# Revit family: Sigma_Compact_DN200-LF_PN16_RFA_2018
name_source: partatom
category: Pipe Accessories
revit_build: Autodesk Revit LT 2018 (Build: 20180329_1100(x64)
units: mm (PartAtom-declared; Revit-internal decimal feet)

## family parameters
Always vertical = Yes
Cut with Voids When Loaded = No
Part Type = Valve - Breaks Into
Round Connector Dimension = Use Diameter
Shared = No
Work Plane-Based = No

## types (9) — shared parameters
CAT0 = Yes
Description = Automatický vyvažovací ventil
H6 = 85 mm
L2D = 230 mm
L2D_Min = 30 mm  [stored 0.0984252 ft]
MC Pressure Drop Maximum Value = 0.0 Pa
MC Pressure Drop Minimum Value = 0.0 Pa
MC Use Limits From Balancing Method = No
Manufacturer = Hydronix
QmdConnectorList = 301;D;302;D
URL = www.hydronix.cz
W2D = 50 mm
magiPartTypeId = 304
magiProductFamilyId = 111bdfd32e424cd9a1e5f1ca7ea2b6
zero-valued in all types: MC Throttling Maximum Value, MC Throttling Minimum Value

## per-type parameters (varying)
- Sigma Compact DN 050 LF PN16: D=50 mm; DF2=83 mm; H=367 mm; H1=480 mm; H11=124 mm; H2=62 mm; H3=21 mm; H4=25 mm  [stored 0.082021 ft]; HDF=202 mm; HDF__ve=-202 mm  [stored -0.66273 ft]; HH1=33 mm  [stored 0.108268 ft]; HH12=17 mm; L2=115 mm; L3=193 mm; L4=108 mm; L42=54 mm; L43=38 mm; L432=19 mm; LF=18 mm; LF2=9 mm; LF__ve=-18 mm; MC Product Code=53-2400 DN50; PN16; (2480-15000 l/h); kvs=34; R1=58 mm; R3=43 mm; R4=40 mm; Type Comments=přírubový; PN16; max dp=800kPa; 0~+120°C; max uzavírací tlak 1MPa; magiProductId=7ce002c265594233b83d195dc264f1
- Sigma Compact DN 065 LF PN16: D=65 mm; DF2=93 mm; H=384 mm; H1=497 mm; H11=139 mm; H2=69 mm; H3=23 mm; H4=28 mm  [stored 0.0918635 ft]; HDF=199 mm; HDF__ve=-199 mm  [stored -0.652887 ft]; HH1=33 mm  [stored 0.108268 ft]; HH12=17 mm; L2=145 mm; L3=244 mm; L4=136 mm; L42=68 mm; L43=48 mm; L432=24 mm  [stored 0.0787402 ft]; LF=23 mm; LF2=12 mm  [stored 0.0393701 ft]; LF__ve=-23 mm; MC Product Code=53-2401 DN65; PN16; (4380-25000 l/h); kvs=50; R1=73 mm; R3=48 mm; R4=51 mm; Type Comments=přírubový; PN16; max dp=800kPa; 0~+120°C; max uzavírací tlak 1MPa; magiProductId=7b440009bc83499eb1c9a6fd3b4fee
- Sigma Compact DN 080 LF PN16: D=80 mm; DF2=100 mm; H=413 mm; H1=526 mm; H11=150 mm; H2=75 mm; H3=25 mm  [stored 0.082021 ft]; H4=30 mm  [stored 0.0984252 ft]; HDF=213 mm; HDF__ve=-213 mm  [stored -0.698819 ft]; HH1=33 mm  [stored 0.108268 ft]; HH12=17 mm; L2=155 mm; L3=260 mm; L4=146 mm; L42=73 mm; L43=51 mm; L432=25 mm  [stored 0.082021 ft]; LF=25 mm  [stored 0.082021 ft]; LF2=12 mm  [stored 0.0393701 ft]; LF__ve=-25 mm  [stored -0.082021 ft]; MC Product Code=53-2402 DN80; PN16; (5340-34000 l/h); kvs=68; R1=78 mm; R3=52 mm; R4=54 mm; Type Comments=přírubový; PN16; max dp=800kPa; 0~+120°C; max uzavírací tlak 1MPa; magiProductId=c04670cd33374e61a046fccc79a79b
- Sigma Compact DN 100 LF PN16: D=100 mm; DF2=118 mm; H=566 mm; H1=714 mm; H11=176 mm; H2=88 mm; H3=29 mm  [stored 0.0951444 ft]; H4=35 mm  [stored 0.114829 ft]; HDF=331 mm; HDF__ve=-331 mm  [stored -1.08596 ft]; HH1=68 mm; HH12=34 mm  [stored 0.111549 ft]; L2=175 mm; L3=294 mm; L4=165 mm; L42=82 mm; L43=58 mm; L432=29 mm  [stored 0.0951444 ft]; LF=28 mm  [stored 0.0918635 ft]; LF2=14 mm  [stored 0.0459318 ft]; LF__ve=-28 mm  [stored -0.0918635 ft]; MC Product Code=53-2403 DN100; PN16; (12100-68000 l/h); kvs=115; R1=88 mm; R3=61 mm; R4=61 mm; Type Comments=přírubový; PN16; max dp=800kPa; 0~+120°C; max uzavírací tlak 1MPa; magiProductId=e9669c3b3cb042d39f52f9a3f8394b
- Sigma Compact DN 125 LF PN16: D=125 mm; DF2=135 mm; H=608 mm; H1=761 mm; H11=203 mm; H2=101 mm; H3=34 mm  [stored 0.111549 ft]; H4=41 mm; HDF=338 mm; HDF__ve=-338 mm  [stored -1.10892 ft]; HH1=73 mm; HH12=37 mm; L2=200 mm; L3=336 mm; L4=188 mm; L42=94 mm; L43=66 mm; L432=33 mm  [stored 0.108268 ft]; LF=32 mm  [stored 0.104987 ft]; LF2=16 mm  [stored 0.0524934 ft]; LF__ve=-32 mm  [stored -0.104987 ft]; MC Product Code=53-2404 DN125; PN16; (18500-110000 l/h); kvs=186; R1=100 mm; R3=70 mm; R4=70 mm; Type Comments=přírubový; PN16; max dp=800kPa; 0~+120°C; max uzavírací tlak 1MPa; magiProductId=72414964175c4f3999d5daaa67221e
- Sigma Compact DN 150 LF PN16: D=150 mm; DF2=143 mm; H=676 mm; H1=782 mm; H11=214 mm; H2=107 mm; H3=36 mm; H4=43 mm; HDF=391 mm; HDF__ve=-391 mm  [stored -1.28281 ft]; HH1=26 mm  [stored 0.0853018 ft]; HH12=13 mm  [stored 0.0426509 ft]; L2=240 mm; L3=403 mm; L4=226 mm; L42=113 mm; L43=79 mm; L432=39 mm; LF=38 mm; LF2=19 mm; LF__ve=-38 mm; MC Product Code=53-2405 DN150; PN16; (25600-148000 l/h); kvs=250; R1=120 mm; R3=74 mm; R4=84 mm; Type Comments=přírubový; PN16; max dp=800kPa; 0~+110°C; max uzavírací tlak 1MPa; magiProductId=cb5ac98de80a46389b4a96eb8539c2
- Sigma Compact DN 200 LF PN16: D=200 mm; DF2=190 mm; H=714 mm; H1=853 mm; H11=285 mm; H2=143 mm; H3=48 mm; H4=57 mm; HDF=334 mm; HDF__ve=-334 mm  [stored -1.0958 ft]; HH1=59 mm; HH12=30 mm  [stored 0.0984252 ft]; L2=300 mm; L3=504 mm; L4=282 mm; L42=141 mm; L43=99 mm; L432=49 mm; LF=48 mm; LF2=24 mm  [stored 0.0787402 ft]; LF__ve=-48 mm  [stored -0.15748 ft]; MC Product Code=53-2406 DN200; PN16; (95000-210000 l/h); kvs=371; R1=150 mm; R3=99 mm; R4=105 mm; Type Comments=přírubový; PN16; max dp=800kPa; 0~+110°C; max uzavírací tlak 1MPa; magiProductId=bd9983fcf82240be8b5626661ef83b
- Sigma Compact DN 250 LF PN16: D=250 mm; DF2=222 mm; H=906 mm; H1=1044 mm; H11=333 mm; H2=167 mm; H3=56 mm; H4=67 mm; HDF=462 mm; HDF__ve=-462 mm  [stored -1.51575 ft]; HH1=58 mm; HH12=29 mm  [stored 0.0951444 ft]; L2=365 mm; L3=613 mm; L4=343 mm; L42=172 mm; L43=120 mm; L432=60 mm; LF=58 mm; LF2=29 mm  [stored 0.0951444 ft]; LF__ve=-58 mm; MC Product Code=53-2407 DN250; PN16; (190000-475000 l/h); kvs=803; R1=183 mm; R3=115 mm; R4=128 mm; Type Comments=přírubový; PN16; max dp=800kPa; 0~+110°C; max uzavírací tlak 1MPa; magiProductId=6516628c9ce0481f89e5702e575104
- Sigma Compact DN 300 LF PN16: D=300 mm; DF2=260 mm; H=944 mm; H1=1082 mm; H11=390 mm; H2=195 mm; H3=65 mm; H4=78 mm; HDF=424 mm; HDF__ve=-424 mm  [stored -1.39108 ft]; HH1=58 mm; HH12=29 mm  [stored 0.0951444 ft]; L2=425 mm; L3=714 mm; L4=400 mm; L42=200 mm; L43=140 mm; L432=70 mm; LF=68 mm; LF2=34 mm  [stored 0.111549 ft]; LF__ve=-68 mm  [stored -0.223097 ft]; MC Product Code=53-2408 DN300; PN16; (190000-475000 l/h); kvs=803; R1=213 mm; R3=135 mm; R4=149 mm; Type Comments=přírubový; PN16; max dp=800kPa; 0~+110°C; max uzavírací tlak 1MPa; magiProductId=f16ecb3a8ad443e99405ecd1e4779a

note: [stored X ft] marks values corroborated as IEEE doubles in the binary element streams (Revit-internal decimal feet)

## geometry (parser evidence)
native form markers: Sweep x1
no freeform markers — native parametric forms only
